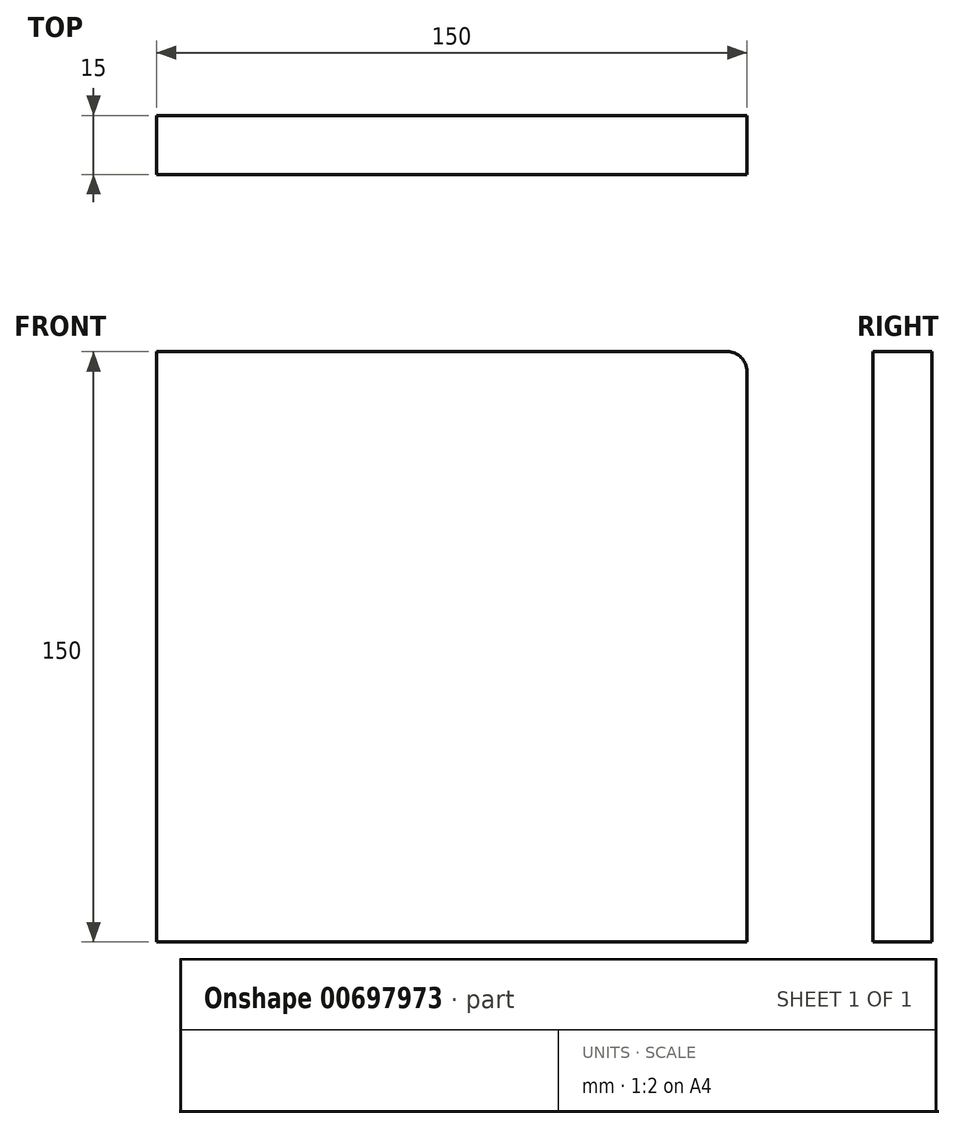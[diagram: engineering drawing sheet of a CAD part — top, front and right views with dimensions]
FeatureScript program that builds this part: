
annotation { "Feature Type Name" : "Feature", "Feature Type Description" : "" }
export const myFeature = defineFeature(function(context is Context, id is Id, definition is map)
    precondition{}
    {
        {
            var Q0;
            Q0=qCreatedBy(makeId("Front.planeOp"),FACE);
            var sketch = newSketch(context, id + "F0", { "sketchPlane" : qUnion([Q0])});
            skLineSegment(sketch, "E0.bottom", {"start": v(75, -75) * mm, "end": v(-75, -75) * mm});
            skLineSegment(sketch, "E0.top", {"start": v(75, 75) * mm, "end": v(-75, 75) * mm});
            skLineSegment(sketch, "E0.left", {"start": v(75, -75) * mm, "end": v(75, 75) * mm});
            skLineSegment(sketch, "E0.right", {"start": v(-75, -75) * mm, "end": v(-75, 75) * mm});
            skPoint(sketch, "E0.middle", {"position": v(0, 0) * mm});
            skSolve(sketch);
        }
        {
            var Q0;
            Q0=makeQuery(id+"F0.imprint","IMPRINT",FACE,{"disambiguationData":[TD([[makeQuery(id+"F0.imprint","IMPRINT",EDGE,{"derivedFrom":sQuery(id+"F0.wireOp",EDGE,"E0.bottom")}),-1.0]])]});
            extrude(context, id + "F1", {"entities" : qUnion([Q0]), "depth" : 15 * mm, "offsetDistance" : 25 * mm});
        }
        {
            var Q0;
            Q0=makeQuery(id+"F1.opExtrude","SWEPT_EDGE",EDGE,{"disambiguationData":[OSD([sQuery(id+"F0.wireOp",EDGE,"E0.top"),sQuery(id+"F0.wireOp",EDGE,"E0.left")])]});
            fillet(context, id + "F2", {"entities" : qUnion([Q0]), "radius" : 5 * mm, "tangentPropagation" : true, "allowEdgeOverflow" : false});
        }
    });
